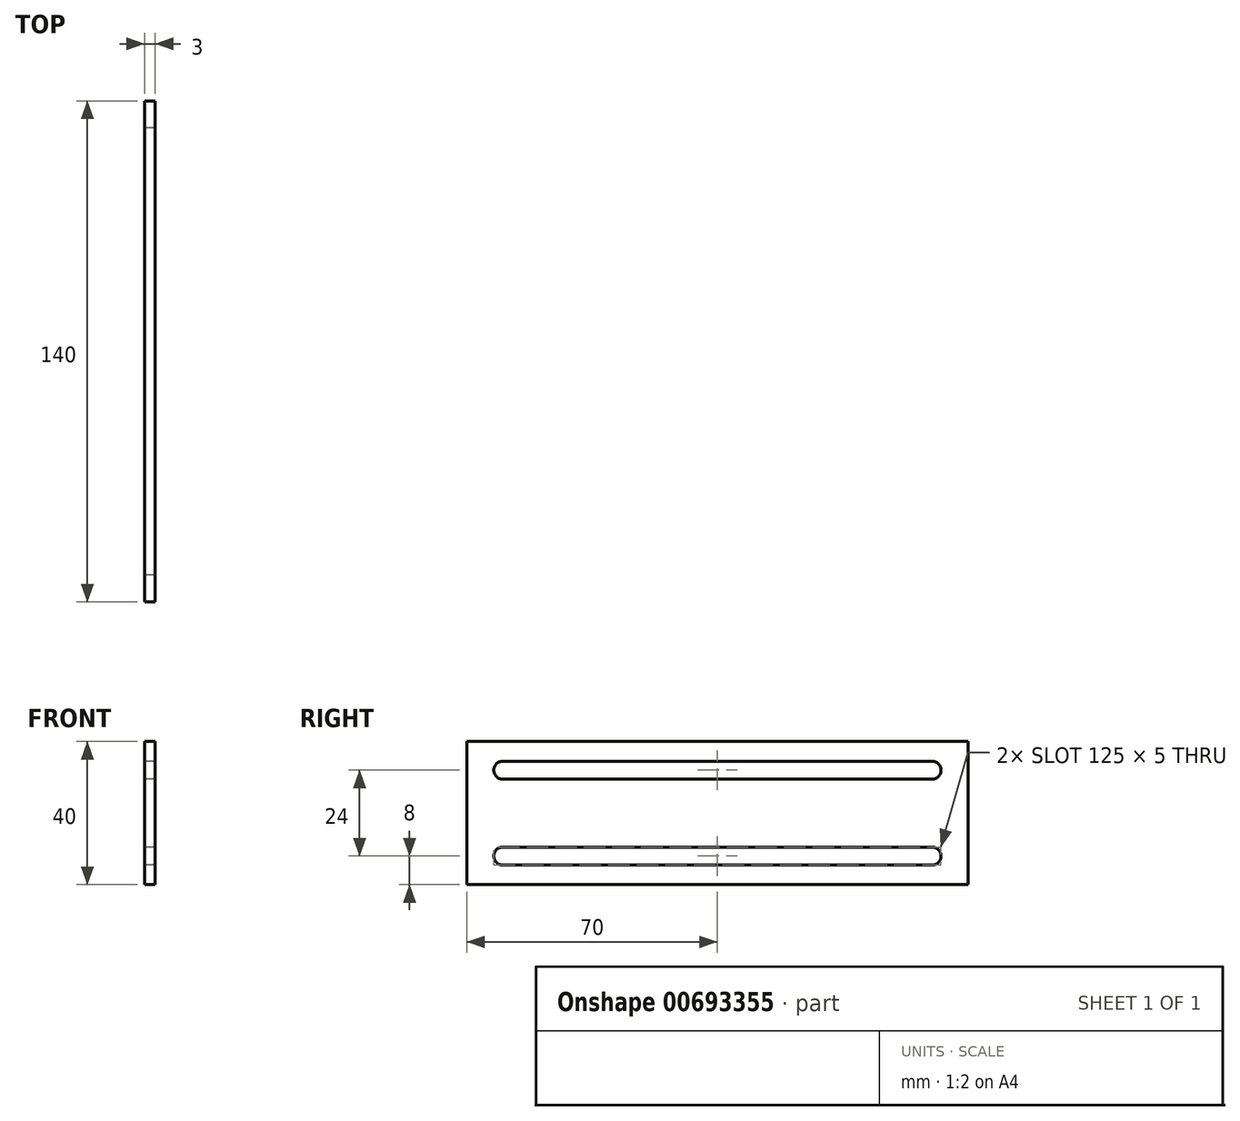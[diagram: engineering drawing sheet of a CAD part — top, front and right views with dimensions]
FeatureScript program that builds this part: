
annotation { "Feature Type Name" : "Feature", "Feature Type Description" : "" }
export const myFeature = defineFeature(function(context is Context, id is Id, definition is map)
    precondition{}
    {
        {
            var Q0;
            Q0=qCreatedBy(makeId("Right.planeOp"),FACE);
            var sketch = newSketch(context, id + "F0", { "sketchPlane" : qUnion([Q0])});
            skLineSegment(sketch, "E0.bottom", {"start": v(-140, 20) * mm, "end": v(0, 20) * mm});
            skLineSegment(sketch, "E0.top", {"start": v(-140, -20) * mm, "end": v(0, -20) * mm});
            skLineSegment(sketch, "E0.left", {"start": v(-140, 20) * mm, "end": v(-140, -20) * mm});
            skLineSegment(sketch, "E0.right", {"start": v(0, 20) * mm, "end": v(0, -20) * mm});
            skLineSegment(sketch, "E1.bottom", {"start": v(-130, 14.5) * mm, "end": v(-10, 14.5) * mm});
            skLineSegment(sketch, "E1.top", {"start": v(-130, 9.5) * mm, "end": v(-10, 9.5) * mm});
            skLineSegment(sketch, "E1.left", {"start": v(-130, 14.5) * mm, "end": v(-130, 9.5) * mm});
            skLineSegment(sketch, "E1.right", {"start": v(-10, 14.5) * mm, "end": v(-10, 9.5) * mm});
            skLineSegment(sketch, "E2.bottom", {"start": v(-130, -9.5) * mm, "end": v(-10, -9.5) * mm});
            skLineSegment(sketch, "E2.top", {"start": v(-130, -14.5) * mm, "end": v(-10, -14.5) * mm});
            skLineSegment(sketch, "E2.left", {"start": v(-130, -9.5) * mm, "end": v(-130, -14.5) * mm});
            skLineSegment(sketch, "E2.right", {"start": v(-10, -9.5) * mm, "end": v(-10, -14.5) * mm});
            skArc(sketch, "E3", {"start": v(-130, 14.5) * mm, "mid": v(-132.5, 12) * mm, "end": v(-130, 9.5) * mm});
            skArc(sketch, "E4", {"start": v(-10, 14.5) * mm, "mid": v(-7.5, 12) * mm, "end": v(-10, 9.5) * mm});
            skArc(sketch, "E5", {"start": v(-130, -9.5) * mm, "mid": v(-132.5, -12) * mm, "end": v(-130, -14.5) * mm});
            skArc(sketch, "E6", {"start": v(-10, -9.5) * mm, "mid": v(-7.5, -12) * mm, "end": v(-10, -14.5) * mm});
            skSolve(sketch);
        }
        {
            var Q0;
            Q0=qSketchRegion(id+"F0",true);
            extrude(context, id + "F1", {"entities" : qUnion([Q0]), "depth" : 3 * mm, "offsetDistance" : 25 * mm});
        }
    });
